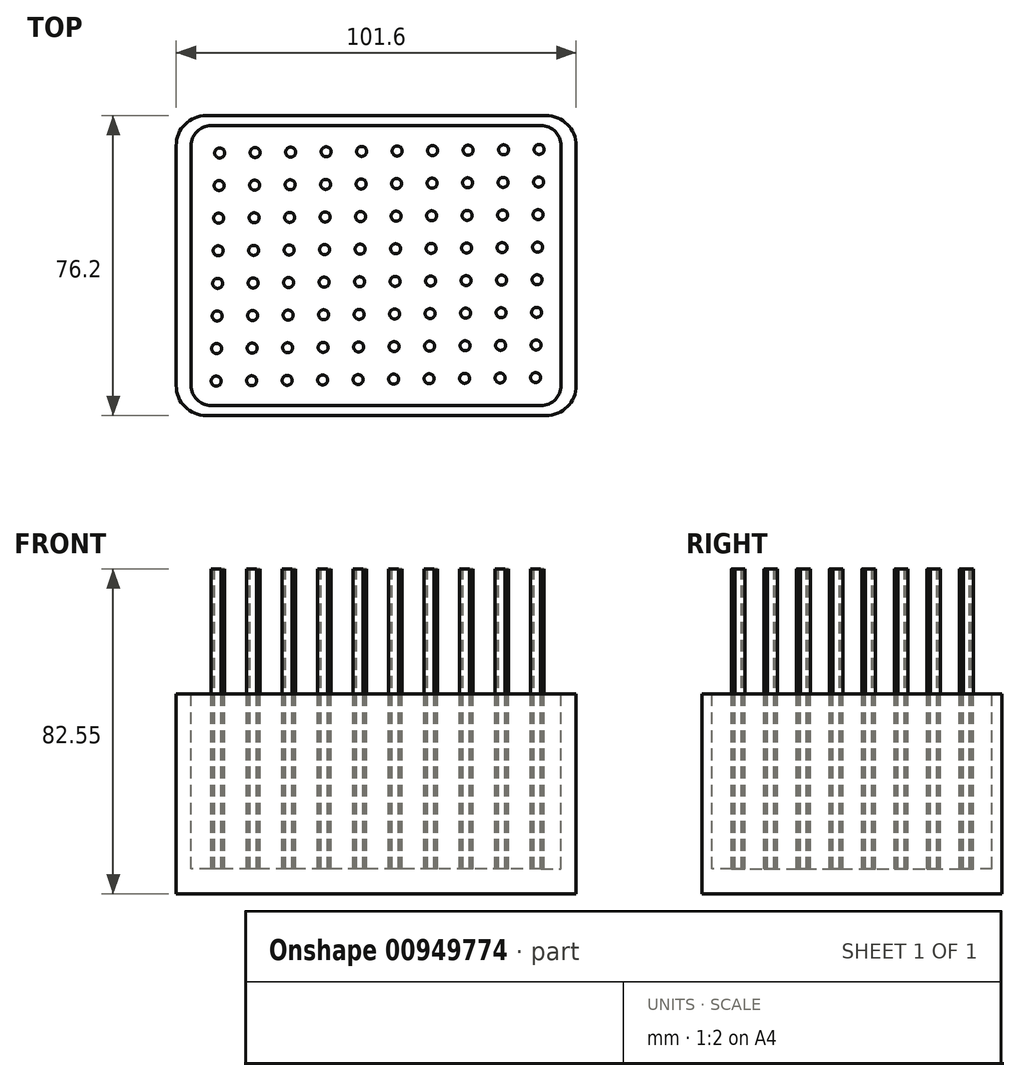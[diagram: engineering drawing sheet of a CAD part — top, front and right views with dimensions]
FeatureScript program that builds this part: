
annotation { "Feature Type Name" : "Feature", "Feature Type Description" : "" }
export const myFeature = defineFeature(function(context is Context, id is Id, definition is map)
    precondition{}
    {
        {
            var Q0;
            Q0=qCreatedBy(makeId("Top.planeOp"),FACE);
            var sketch = newSketch(context, id + "F0", { "sketchPlane" : qUnion([Q0])});
            skLineSegment(sketch, "E0.bottom", {"start": v(-43.18, 38.1) * mm, "end": v(43.18, 38.1) * mm});
            skLineSegment(sketch, "E0.top", {"start": v(-43.18, -38.1) * mm, "end": v(43.18, -38.1) * mm});
            skLineSegment(sketch, "E0.left", {"start": v(-50.8, 30.48) * mm, "end": v(-50.8, -30.48) * mm});
            skLineSegment(sketch, "E0.right", {"start": v(50.8, 30.48) * mm, "end": v(50.8, -30.48) * mm});
            skLineSegment(sketch, "E1.bottom", {"start": v(0, 38.1) * mm, "end": v(0, 38.1) * mm});
            skLineSegment(sketch, "E1.top", {"start": v(0, -38.1) * mm, "end": v(0, -38.1) * mm});
            skLineSegment(sketch, "E1.left", {"start": v(0, 38.1) * mm, "end": v(0, -38.1) * mm, "construction": true});
            skLineSegment(sketch, "E1.right", {"start": v(0, 38.1) * mm, "end": v(0, -38.1) * mm, "construction": true});
            skLineSegment(sketch, "E2.bottom", {"start": v(-50.8, 0) * mm, "end": v(50.8, 0) * mm, "construction": true});
            skLineSegment(sketch, "E2.top", {"start": v(-50.8, 0) * mm, "end": v(50.8, 0) * mm, "construction": true});
            skLineSegment(sketch, "E2.left", {"start": v(-50.8, 0) * mm, "end": v(-50.8, 0) * mm});
            skLineSegment(sketch, "E2.right", {"start": v(50.8, 0) * mm, "end": v(50.8, 0) * mm});
            skPoint(sketch, "E3.visualSharp", {"position": v(-50.8, 38.1) * mm});
            skArc(sketch, "E3.filletArc", {"start": v(-43.18, 38.1) * mm, "mid": v(-48.57, 35.87) * mm, "end": v(-50.8, 30.48) * mm});
            skPoint(sketch, "E4.visualSharp", {"position": v(-50.8, -38.1) * mm});
            skArc(sketch, "E4.filletArc", {"start": v(-50.8, -30.48) * mm, "mid": v(-48.57, -35.87) * mm, "end": v(-43.18, -38.1) * mm});
            skPoint(sketch, "E5.visualSharp", {"position": v(50.8, -38.1) * mm});
            skArc(sketch, "E5.filletArc", {"start": v(43.18, -38.1) * mm, "mid": v(48.57, -35.87) * mm, "end": v(50.8, -30.48) * mm});
            skPoint(sketch, "E6.visualSharp", {"position": v(50.8, 38.1) * mm});
            skArc(sketch, "E6.filletArc", {"start": v(50.8, 30.48) * mm, "mid": v(48.57, 35.87) * mm, "end": v(43.18, 38.1) * mm});
            skSolve(sketch);
        }
        {
            var Q0;
            Q0=makeQuery(id+"F0.imprint","IMPRINT",FACE,{"disambiguationData":[TD([[makeQuery(id+"F0.imprint","IMPRINT",EDGE,{"derivedFrom":sQuery(id+"F0.wireOp",EDGE,"E0.bottom")}),-1.0]])]});
            extrude(context, id + "F1", {"entities" : qUnion([Q0]), "depth" : 6.35 * mm, "offsetDistance" : 25.4 * mm});
        }
        {
            var Q0;
            Q0=qCreatedBy(makeId("Top.planeOp"),FACE);
            var sketch = newSketch(context, id + "F2", { "sketchPlane" : qUnion([Q0])});
            skArc(sketch, "E7.0.0", {"start": v(-50.8, -30.48) * mm, "mid": v(-48.57, -35.87) * mm, "end": v(-43.18, -38.1) * mm});
            skLineSegment(sketch, "E7.0.1", {"start": v(-43.18, -38.1) * mm, "end": v(43.18, -38.1) * mm});
            skArc(sketch, "E7.0.2", {"start": v(43.18, -38.1) * mm, "mid": v(48.57, -35.87) * mm, "end": v(50.8, -30.48) * mm});
            skLineSegment(sketch, "E7.0.3", {"start": v(50.8, -30.48) * mm, "end": v(50.8, 30.48) * mm});
            skArc(sketch, "E7.0.4", {"start": v(50.8, 30.48) * mm, "mid": v(48.57, 35.87) * mm, "end": v(43.18, 38.1) * mm});
            skLineSegment(sketch, "E7.0.5", {"start": v(43.18, 38.1) * mm, "end": v(-43.18, 38.1) * mm});
            skArc(sketch, "E7.0.6", {"start": v(-43.18, 38.1) * mm, "mid": v(-48.57, 35.87) * mm, "end": v(-50.8, 30.48) * mm});
            skLineSegment(sketch, "E7.0.7", {"start": v(-50.8, 30.48) * mm, "end": v(-50.8, -30.48) * mm});
            skLineSegment(sketch, "E8.0", {"start": v(-47, 30.48) * mm, "end": v(-47, -30.48) * mm});
            skLineSegment(sketch, "E8.3", {"start": v(41.91, 35.56) * mm, "end": v(-41.91, 35.56) * mm});
            skLineSegment(sketch, "E8.4", {"start": v(-41.91, -35.56) * mm, "end": v(41.9, -35.56) * mm});
            skLineSegment(sketch, "E8.6", {"start": v(46.99, -30.48) * mm, "end": v(47, 30.48) * mm});
            skArc(sketch, "E9.filletArc", {"start": v(-41.91, 35.56) * mm, "mid": v(-45.5, 34.07) * mm, "end": v(-47, 30.48) * mm});
            skArc(sketch, "E10.filletArc", {"start": v(47, 30.48) * mm, "mid": v(45.5, 34.07) * mm, "end": v(41.91, 35.56) * mm});
            skArc(sketch, "E11.filletArc", {"start": v(-47, -30.48) * mm, "mid": v(-45.5, -34.07) * mm, "end": v(-41.91, -35.56) * mm});
            skArc(sketch, "E12.filletArc", {"start": v(41.9, -35.56) * mm, "mid": v(45.5, -34.07) * mm, "end": v(47, -30.48) * mm});
            skSolve(sketch);
        }
        {
            var Q0;
            Q0 = qSketchRegion(id + "F2", true);
            extrude(context, id + "F3", {"entities" : qUnion([Q0]), "operationType" : NewBodyOperationType.ADD, "depth" : 50.8 * mm, "offsetDistance" : 25.4 * mm});
        }
        {
            var Q0;
            Q0=makeQuery(id+"F1.opExtrude","CAP_FACE",FACE,{"disambiguationData":[OSD([sQuery(id+"F0.wireOp",EDGE,"E0.bottom"),sQuery(id+"F0.wireOp",EDGE,"E0.top"),sQuery(id+"F0.wireOp",EDGE,"E0.left"),sQuery(id+"F0.wireOp",EDGE,"E0.right"),sQuery(id+"F0.wireOp",EDGE,"E3.filletArc"),sQuery(id+"F0.wireOp",EDGE,"E4.filletArc"),sQuery(id+"F0.wireOp",EDGE,"E5.filletArc"),sQuery(id+"F0.wireOp",EDGE,"E6.filletArc")])],"isStart":false});
            var sketch = newSketch(context, id + "F4", { "sketchPlane" : qUnion([Q0])});
            skSolve(sketch);
        }
        {
            var Q0;
            {var subQ0=makeQuery(id+"F1.opExtrude","CAP_FACE",FACE,{"disambiguationData":[OSD([sQuery(id+"F0.wireOp",EDGE,"E0.bottom"),sQuery(id+"F0.wireOp",EDGE,"E0.top"),sQuery(id+"F0.wireOp",EDGE,"E0.left"),sQuery(id+"F0.wireOp",EDGE,"E0.right"),sQuery(id+"F0.wireOp",EDGE,"E3.filletArc"),sQuery(id+"F0.wireOp",EDGE,"E4.filletArc"),sQuery(id+"F0.wireOp",EDGE,"E5.filletArc"),sQuery(id+"F0.wireOp",EDGE,"E6.filletArc")])],"isStart":false});Q0=makeQuery(id+"F4.imprint","IMPRINT",FACE,{"disambiguationData":[TD([[makeQuery(id+"F4.imprint","IMPRINT",EDGE,{"derivedFrom":makeQuery(id+"F3.boolean.opBoolean","INTERSECT",EDGE,{"derivedFrom":[subQ0,makeQuery(id+"F3.opExtrude","SWEPT_FACE",FACE,{"disambiguationData":[OSD([sQuery(id+"F2.wireOp",EDGE,"E8.0")])]})]})}),-1.0]])]});}
            extrude(context, id + "F5", {"entities" : qUnion([Q0]), "operationType" : NewBodyOperationType.ADD, "depth" : 76.2 * mm, "offsetDistance" : 25.4 * mm});
        }
        {
            var Q0;
            Q0=makeQuery(id+"F5.opExtrude","CAP_FACE",FACE,{"disambiguationData":[OSD([sQuery(id+"F0.wireOp",EDGE,"E0.bottom"),sQuery(id+"F0.wireOp",EDGE,"E0.top"),sQuery(id+"F0.wireOp",EDGE,"E0.left"),sQuery(id+"F0.wireOp",EDGE,"E0.right"),sQuery(id+"F0.wireOp",EDGE,"E3.filletArc"),sQuery(id+"F0.wireOp",EDGE,"E4.filletArc"),sQuery(id+"F0.wireOp",EDGE,"E5.filletArc"),sQuery(id+"F0.wireOp",EDGE,"E6.filletArc"),sQuery(id+"F2.wireOp",EDGE,"E8.0"),sQuery(id+"F2.wireOp",EDGE,"E8.3"),sQuery(id+"F2.wireOp",EDGE,"E8.4"),sQuery(id+"F2.wireOp",EDGE,"E8.6"),sQuery(id+"F2.wireOp",EDGE,"E9.filletArc"),sQuery(id+"F2.wireOp",EDGE,"E10.filletArc"),sQuery(id+"F2.wireOp",EDGE,"E11.filletArc"),sQuery(id+"F2.wireOp",EDGE,"E12.filletArc")])],"isStart":false});
            var sketch = newSketch(context, id + "F6", { "sketchPlane" : qUnion([Q0])});
            skCircle(sketch, "E13", {"center": v(-39.75, 28.6) * mm, "radius": 1.27 * mm});
            skCircle(sketch, "E14.0.1.0", {"center": v(-39.88, 20.32) * mm, "radius": 1.27 * mm});
            skCircle(sketch, "E14.0.2.0", {"center": v(-40, 12.04) * mm, "radius": 1.27 * mm});
            skCircle(sketch, "E14.0.3.0", {"center": v(-40.13, 3.76) * mm, "radius": 1.27 * mm});
            skCircle(sketch, "E14.0.4.0", {"center": v(-40.26, -4.52) * mm, "radius": 1.27 * mm});
            skCircle(sketch, "E14.0.5.0", {"center": v(-40.38, -12.8) * mm, "radius": 1.27 * mm});
            skCircle(sketch, "E14.0.6.0", {"center": v(-40.51, -21.09) * mm, "radius": 1.27 * mm});
            skCircle(sketch, "E14.0.7.0", {"center": v(-40.64, -29.37) * mm, "radius": 1.27 * mm});
            skCircle(sketch, "E14.1.0.0", {"center": v(-30.73, 28.7) * mm, "radius": 1.27 * mm});
            skCircle(sketch, "E14.1.1.0", {"center": v(-30.86, 20.42) * mm, "radius": 1.27 * mm});
            skCircle(sketch, "E14.1.2.0", {"center": v(-30.99, 12.14) * mm, "radius": 1.27 * mm});
            skCircle(sketch, "E14.1.3.0", {"center": v(-31.11, 3.86) * mm, "radius": 1.27 * mm});
            skCircle(sketch, "E14.1.4.0", {"center": v(-31.24, -4.42) * mm, "radius": 1.27 * mm});
            skCircle(sketch, "E14.1.5.0", {"center": v(-31.37, -12.7) * mm, "radius": 1.27 * mm});
            skCircle(sketch, "E14.1.6.0", {"center": v(-31.5, -20.99) * mm, "radius": 1.27 * mm});
            skCircle(sketch, "E14.1.7.0", {"center": v(-31.62, -29.27) * mm, "radius": 1.27 * mm});
            skCircle(sketch, "E14.2.0.0", {"center": v(-21.72, 28.8) * mm, "radius": 1.27 * mm});
            skCircle(sketch, "E14.2.1.0", {"center": v(-21.84, 20.52) * mm, "radius": 1.27 * mm});
            skCircle(sketch, "E14.2.2.0", {"center": v(-21.97, 12.24) * mm, "radius": 1.27 * mm});
            skCircle(sketch, "E14.2.3.0", {"center": v(-22.1, 3.96) * mm, "radius": 1.27 * mm});
            skCircle(sketch, "E14.2.4.0", {"center": v(-22.22, -4.32) * mm, "radius": 1.27 * mm});
            skCircle(sketch, "E14.2.5.0", {"center": v(-22.35, -12.6) * mm, "radius": 1.27 * mm});
            skCircle(sketch, "E14.2.6.0", {"center": v(-22.48, -20.89) * mm, "radius": 1.27 * mm});
            skCircle(sketch, "E14.2.7.0", {"center": v(-22.6, -29.17) * mm, "radius": 1.27 * mm});
            skCircle(sketch, "E14.3.0.0", {"center": v(-12.7, 28.9) * mm, "radius": 1.27 * mm});
            skCircle(sketch, "E14.3.1.0", {"center": v(-12.83, 20.62) * mm, "radius": 1.27 * mm});
            skCircle(sketch, "E14.3.2.0", {"center": v(-12.95, 12.34) * mm, "radius": 1.27 * mm});
            skCircle(sketch, "E14.3.3.0", {"center": v(-13.08, 4.06) * mm, "radius": 1.27 * mm});
            skCircle(sketch, "E14.3.4.0", {"center": v(-13.2, -4.22) * mm, "radius": 1.27 * mm});
            skCircle(sketch, "E14.3.5.0", {"center": v(-13.33, -12.5) * mm, "radius": 1.27 * mm});
            skCircle(sketch, "E14.3.6.0", {"center": v(-13.46, -20.79) * mm, "radius": 1.27 * mm});
            skCircle(sketch, "E14.3.7.0", {"center": v(-13.58, -29.07) * mm, "radius": 1.27 * mm});
            skCircle(sketch, "E14.4.0.0", {"center": v(-3.68, 29) * mm, "radius": 1.27 * mm});
            skCircle(sketch, "E14.4.1.0", {"center": v(-3.8, 20.72) * mm, "radius": 1.27 * mm});
            skCircle(sketch, "E14.4.2.0", {"center": v(-3.93, 12.44) * mm, "radius": 1.27 * mm});
            skCircle(sketch, "E14.4.3.0", {"center": v(-4.06, 4.16) * mm, "radius": 1.27 * mm});
            skCircle(sketch, "E14.4.4.0", {"center": v(-4.19, -4.12) * mm, "radius": 1.27 * mm});
            skCircle(sketch, "E14.4.5.0", {"center": v(-4.31, -12.4) * mm, "radius": 1.27 * mm});
            skCircle(sketch, "E14.4.6.0", {"center": v(-4.44, -20.69) * mm, "radius": 1.27 * mm});
            skCircle(sketch, "E14.4.7.0", {"center": v(-4.57, -28.97) * mm, "radius": 1.27 * mm});
            skCircle(sketch, "E14.5.0.0", {"center": v(5.34, 29.1) * mm, "radius": 1.27 * mm});
            skCircle(sketch, "E14.5.1.0", {"center": v(5.2, 20.82) * mm, "radius": 1.27 * mm});
            skCircle(sketch, "E14.5.2.0", {"center": v(5.08, 12.54) * mm, "radius": 1.27 * mm});
            skCircle(sketch, "E14.5.3.0", {"center": v(4.96, 4.26) * mm, "radius": 1.27 * mm});
            skCircle(sketch, "E14.5.4.0", {"center": v(4.83, -4.02) * mm, "radius": 1.27 * mm});
            skCircle(sketch, "E14.5.5.0", {"center": v(4.7, -12.3) * mm, "radius": 1.27 * mm});
            skCircle(sketch, "E14.5.6.0", {"center": v(4.58, -20.58) * mm, "radius": 1.27 * mm});
            skCircle(sketch, "E14.5.7.0", {"center": v(4.45, -28.87) * mm, "radius": 1.27 * mm});
            skCircle(sketch, "E14.6.0.0", {"center": v(14.35, 29.2) * mm, "radius": 1.27 * mm});
            skCircle(sketch, "E14.6.1.0", {"center": v(14.23, 20.92) * mm, "radius": 1.27 * mm});
            skCircle(sketch, "E14.6.2.0", {"center": v(14.1, 12.64) * mm, "radius": 1.27 * mm});
            skCircle(sketch, "E14.6.3.0", {"center": v(13.97, 4.36) * mm, "radius": 1.27 * mm});
            skCircle(sketch, "E14.6.4.0", {"center": v(13.85, -3.92) * mm, "radius": 1.27 * mm});
            skCircle(sketch, "E14.6.5.0", {"center": v(13.72, -12.2) * mm, "radius": 1.27 * mm});
            skCircle(sketch, "E14.6.6.0", {"center": v(13.6, -20.48) * mm, "radius": 1.27 * mm});
            skCircle(sketch, "E14.6.7.0", {"center": v(13.47, -28.77) * mm, "radius": 1.27 * mm});
            skCircle(sketch, "E14.7.0.0", {"center": v(23.37, 29.3) * mm, "radius": 1.27 * mm});
            skCircle(sketch, "E14.7.1.0", {"center": v(23.24, 21.02) * mm, "radius": 1.27 * mm});
            skCircle(sketch, "E14.7.2.0", {"center": v(23.12, 12.74) * mm, "radius": 1.27 * mm});
            skCircle(sketch, "E14.7.3.0", {"center": v(23, 4.46) * mm, "radius": 1.27 * mm});
            skCircle(sketch, "E14.7.4.0", {"center": v(22.86, -3.82) * mm, "radius": 1.27 * mm});
            skCircle(sketch, "E14.7.5.0", {"center": v(22.74, -12.1) * mm, "radius": 1.27 * mm});
            skCircle(sketch, "E14.7.6.0", {"center": v(22.61, -20.38) * mm, "radius": 1.27 * mm});
            skCircle(sketch, "E14.7.7.0", {"center": v(22.49, -28.67) * mm, "radius": 1.27 * mm});
            skCircle(sketch, "E14.8.0.0", {"center": v(32.39, 29.4) * mm, "radius": 1.27 * mm});
            skCircle(sketch, "E14.8.1.0", {"center": v(32.26, 21.12) * mm, "radius": 1.27 * mm});
            skCircle(sketch, "E14.8.2.0", {"center": v(32.14, 12.84) * mm, "radius": 1.27 * mm});
            skCircle(sketch, "E14.8.3.0", {"center": v(32, 4.56) * mm, "radius": 1.27 * mm});
            skCircle(sketch, "E14.8.4.0", {"center": v(31.88, -3.72) * mm, "radius": 1.27 * mm});
            skCircle(sketch, "E14.8.5.0", {"center": v(31.76, -12) * mm, "radius": 1.27 * mm});
            skCircle(sketch, "E14.8.6.0", {"center": v(31.63, -20.28) * mm, "radius": 1.27 * mm});
            skCircle(sketch, "E14.8.7.0", {"center": v(31.5, -28.56) * mm, "radius": 1.27 * mm});
            skCircle(sketch, "E14.9.0.0", {"center": v(41.4, 29.5) * mm, "radius": 1.27 * mm});
            skCircle(sketch, "E14.9.1.0", {"center": v(41.28, 21.22) * mm, "radius": 1.27 * mm});
            skCircle(sketch, "E14.9.2.0", {"center": v(41.15, 12.94) * mm, "radius": 1.27 * mm});
            skCircle(sketch, "E14.9.3.0", {"center": v(41.03, 4.66) * mm, "radius": 1.27 * mm});
            skCircle(sketch, "E14.9.4.0", {"center": v(40.9, -3.62) * mm, "radius": 1.27 * mm});
            skCircle(sketch, "E14.9.5.0", {"center": v(40.77, -11.9) * mm, "radius": 1.27 * mm});
            skCircle(sketch, "E14.9.6.0", {"center": v(40.65, -20.18) * mm, "radius": 1.27 * mm});
            skCircle(sketch, "E14.9.7.0", {"center": v(40.52, -28.46) * mm, "radius": 1.27 * mm});
            skLineSegment(sketch, "E14.direction1", {"start": v(-39.75, 28.6) * mm, "end": v(-30.73, 28.7) * mm, "construction": true});
            skLineSegment(sketch, "E14.direction2", {"start": v(-39.75, 28.6) * mm, "end": v(-39.88, 20.32) * mm, "construction": true});
            skSolve(sketch);
        }
        {
            var Q0;
            Q0=makeQuery(id+"F6.imprint","IMPRINT",FACE,{"disambiguationData":[TD([[makeQuery(id+"F6.imprint","IMPRINT",EDGE,{"derivedFrom":sQuery(id+"F6.wireOp",EDGE,"E13")}),-1.0]])]});
            extrude(context, id + "F7", {"entities" : qUnion([Q0]), "operationType" : NewBodyOperationType.REMOVE, "oppositeDirection" : true, "depth" : 76.2 * mm, "offsetDistance" : 25.4 * mm});
        }
    });
